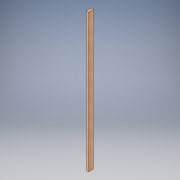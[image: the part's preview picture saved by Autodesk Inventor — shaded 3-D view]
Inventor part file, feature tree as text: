
AUTODESK INVENTOR PART (.ipt)
format: ipt  version: 2017 (Build 210142000, 142)  size: 122,368 bytes
history: native  units: in
note: dims shown in document units (in); Inventor stores cm internally (conversion verified against a paired STEP export)
features: extrude x3, sketch x3
ambient origin geometry x8: Origin, YZ Plane, XZ Plane, XY Plane, X Axis, Y Axis, Z Axis, Center Point
bodies: Solid1 (feature_tree)
feature tree (6):
  extrude  "Extrusion1"  Depth=3.5in
  extrude  "Extrusion4"  Depth=94.5in
  extrude  "Extrusion5"  Depth=1.5in
  sketch  "Sketch1"  dims[d0=1.5in d1=3.5in]
  sketch  "Sketch4"  dims[d2=94.5in d3=0.0in d12=0.1875in]
  sketch  "Sketch5"  dims[d13=1.5in d14=0.0in d15=1.5in d16=0.1875in d17=1.5in d18=0.0in]
